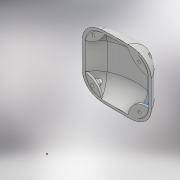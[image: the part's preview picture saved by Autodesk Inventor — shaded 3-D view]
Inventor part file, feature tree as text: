
AUTODESK INVENTOR PART (.ipt)
format: ipt  version: 2017 (Build 210142000, 142)  size: 1,438,208 bytes
history: native  units: mm
features: sketch x12, extrude x11, projected_geometry x9, other x3, plane x1
ambient origin geometry x8: Origin, YZ Plane, XZ Plane, XY Plane, X Axis, Y Axis, Z Axis, Center Point
bodies: Solid1 (feature_tree)
feature tree (36):
  other  "Cabeza0.ipt"
  extrude  "Extrusion11"  Depth=0.2mm TaperAngle=0.0deg
  extrude  "Extrusion12"  Depth=90.0mm TaperAngle=0.0deg
  extrude  "Extrusion18"  Depth=38.025mm
  sketch  "Sketch33"  dims[d80=4.0mm d81=0.0mm d82=36.35mm]
  extrude  "Extrusion19"  Depth=36.35mm
  extrude  "Extrusion20"  Depth=190.0mm TaperAngle=0.0deg
  extrude  "Extrusion21"  Depth=30.0mm TaperAngle=0.0deg
  extrude  "Extrusion22"  Depth=20.0mm
  extrude  "Extrusion23"  Depth=20.0mm TaperAngle=0.0deg
  plane  "Work Plane1"
  extrude  "Extrusion24"  Depth=5.0mm
  extrude  "Extrusion25"  Depth=5.0mm
  extrude  "Extrusion26"  Depth=20.0mm TaperAngle=0.0deg
  other  "Solid1::Cabeza0.ipt"
  other  "TaggingFeature1"
  sketch  "Sketch12"  dims[d0=13.0mm d56=0.2mm d57=0.0mm]
  projected_geometry  "Projected Loop9"
  projected_geometry  "Projected Loop10"
  sketch  "Sketch14"  dims[d58=0.76969mm d59=90.0mm d60=0.0mm]
  projected_geometry  "Projected Loop11"
  projected_geometry  "Projected Loop12"
  projected_geometry  "Projected Loop13"
  projected_geometry  "Projected Loop14"
  sketch  "Sketch31"  dims[d76=0.0mm d78=0.0mm d79=38.025mm]
  sketch  "Sketch34"  dims[d83=30.0mm d84=0.0mm d85=190.0mm d86=0.0mm]
  sketch  "Sketch35"  dims[d87=0.1mm d88=0.0mm d89=30.0mm d90=0.0mm]
  sketch  "Sketch36"  dims[d91=20.0mm d92=20.0mm]
  sketch  "Sketch37"  dims[d93=20.0mm d94=2.0mm d95=0.0mm]
  projected_geometry  "Projected Loop17"
  sketch  "Sketch38"  dims[d96=23.5mm d97=5.0mm]
  projected_geometry  "Projected Loop18"
  sketch  "Sketch39"  dims[d98=5.0mm d99=5.0mm]
  sketch  "Sketch40"  dims[d100=5.0mm d101=20.0mm d102=0.0mm]
  projected_geometry  "Projected Loop19"
  sketch  "Sketch41"  dims[d103=3.0mm d104=3.0mm d105=3.0mm d106=3.0mm d107=2.0mm d108=0.0mm d109=7.0mm d110=7.0mm d111=7.0mm d112=7.0mm d113=3.5mm d114=0.0mm]
